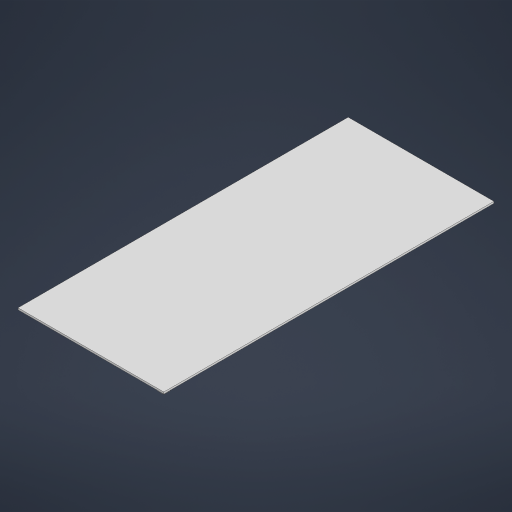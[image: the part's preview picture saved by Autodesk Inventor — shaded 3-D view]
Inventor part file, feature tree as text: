
AUTODESK INVENTOR PART (.ipt)
format: ipt  version: 2024 (Build 280153000, 153)  size: 165,376 bytes
history: native  units: mm
features: extrude x2, sketch x2, other x1
ambient origin geometry x8: Origin, YZ Plane, XZ Plane, XY Plane, X Axis, Y Axis, Z Axis, Center Point
bodies: Body1 (feature_tree)
feature tree (5):
  other  "Sólido1"
  extrude  "Extrusión1"  Depth=1880.0mm
  extrude  "Extrusión2"  Depth=37.0mm
  sketch  "Boceto1"  dims[d0=830.0mm d1=1880.0mm]
  sketch  "Boceto2"  dims[d2=10.0mm d3=0.0mm d4=37.0mm d5=37.0mm d6=1.5mm d7=1.5mm d8=4.0mm d9=0.0mm]
